# Revit family: Shower-Valve_Trim-KOHLER-MODULO-K-37335IN
name_source: partatom
category: Specialty Equipment
revit_build: Autodesk Revit 2017 (Build: 20160225_1515(x64)
units: mm (PartAtom-declared; Revit-internal decimal feet)

## family parameters
Cut with Voids When Loaded = No
Host = Face
OmniClass Number = 23.31.25.00
OmniClass Title = Toilet and Bath Specialties
Part Type = Normal
Room Calculation Point = No
Round Connector Dimension = Use Diameter
Shared = No

## types (2) — shared parameters
ADA Compliant = No
Assembly Code = C1030200
Date Modified = 09/02/2020
Default Elevation = 1067 mm
Description = RECESSED BATH & SHOWER TRIM
Height = 166 mm  [stored 0.544619 ft]
Length = 79 mm
Manufacturer = KOHLER Co.
Master Format 2014 = 10 28 00
Master Format 2014 Name = Toilet, Bath, and Laundry Accessories
Material = Premium Metal Construction
Product Documentation Link = http://resources.kohler.com
Product Name = MODULO
Product Page URL = https://www.kohler.co.in
URL = https://www.kohler.co.in
WaterSense Certified = No
Width = 135 mm  [stored 0.442913 ft]

## per-type parameters (varying)
| type | Finish | Model | Type |
| CP- Polished Chrome | Kohler-Metal-CP-Polished_Chrome | K-37335IN-4FP-CP | 1 |
| AF- French Gold | Kohler-Metal-AF-Vibrant_French_Gold | K-37335IN-4FP-AF | 2 |

note: [stored X ft] marks values corroborated as IEEE doubles in the binary element streams (Revit-internal decimal feet)

## geometry (parser evidence)
native form markers: Sweep x5
no freeform markers — native parametric forms only
